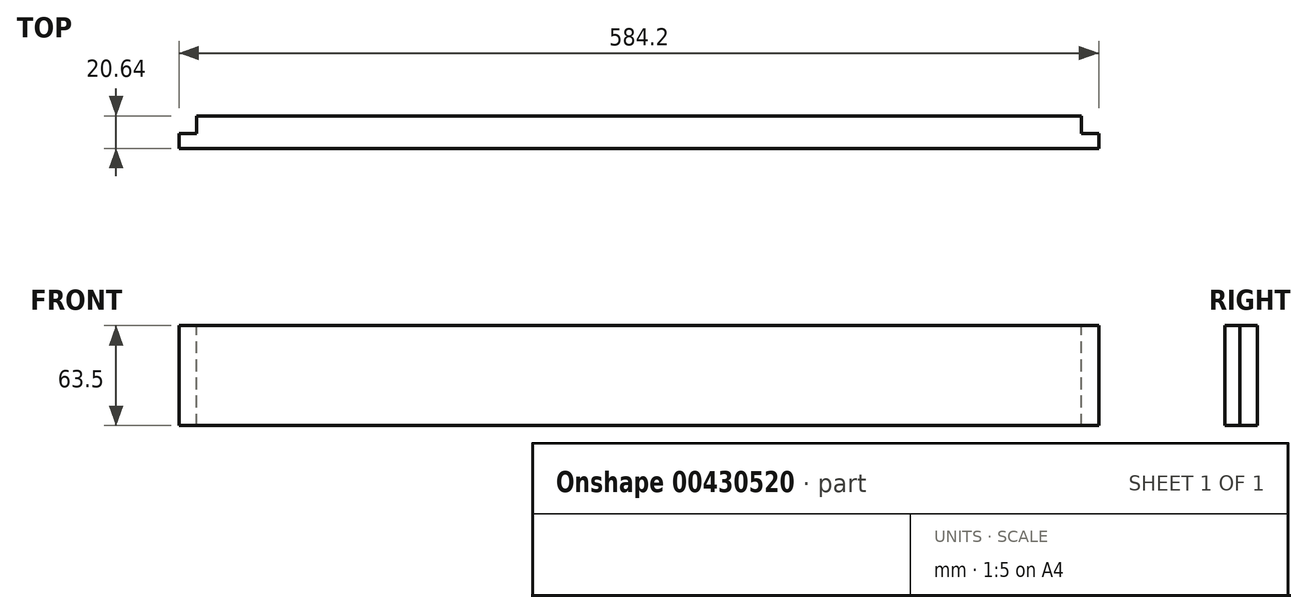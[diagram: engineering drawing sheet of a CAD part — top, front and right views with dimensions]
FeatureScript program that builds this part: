
annotation { "Feature Type Name" : "Feature", "Feature Type Description" : "" }
export const myFeature = defineFeature(function(context is Context, id is Id, definition is map)
    precondition{}
    {
        {
            var Q0;
            Q0=qCreatedBy(makeId("Top.planeOp"),FACE);
            var sketch = newSketch(context, id + "F0", { "sketchPlane" : qUnion([Q0])});
            skLineSegment(sketch, "E0", {"start": v(-292.1, 0) * mm, "end": v(292.1, 0) * mm});
            skLineSegment(sketch, "E1", {"start": v(292.1, 0) * mm, "end": v(292.1, 20.64) * mm});
            skLineSegment(sketch, "E2", {"start": v(292.1, 20.64) * mm, "end": v(-292.1, 20.64) * mm});
            skLineSegment(sketch, "E3", {"start": v(-292.1, 20.64) * mm, "end": v(-292.1, 0) * mm});
            skSolve(sketch);
        }
        {
            var Q0;
            Q0=makeQuery(id+"F0.imprint","IMPRINT",FACE,{"disambiguationData":[TD([[makeQuery(id+"F0.imprint","IMPRINT",EDGE,{"derivedFrom":sQuery(id+"F0.wireOp",EDGE,"E0")}),1.0]])]});
            extrude(context, id + "F1", {"entities" : qUnion([Q0]), "oppositeDirection" : true, "depth" : 63.5 * mm});
        }
        {
            var Q0;
            Q0=makeQuery(id+"F1.opExtrude","CAP_FACE",FACE,{"disambiguationData":[OSD([sQuery(id+"F0.wireOp",EDGE,"E0"),sQuery(id+"F0.wireOp",EDGE,"E1"),sQuery(id+"F0.wireOp",EDGE,"E2"),sQuery(id+"F0.wireOp",EDGE,"E3")])],"isStart":true});
            var sketch = newSketch(context, id + "F2", { "sketchPlane" : qUnion([Q0])});
            skLineSegment(sketch, "E4.bottom", {"start": v(-292.1, 20.64) * mm, "end": v(-280.99, 20.64) * mm});
            skLineSegment(sketch, "E4.top", {"start": v(-292.1, 9.52) * mm, "end": v(-280.99, 9.52) * mm});
            skLineSegment(sketch, "E4.left", {"start": v(-292.1, 20.64) * mm, "end": v(-292.1, 9.52) * mm});
            skLineSegment(sketch, "E4.right", {"start": v(-280.99, 20.64) * mm, "end": v(-280.99, 9.52) * mm});
            skLineSegment(sketch, "E5.bottom", {"start": v(292.1, 20.64) * mm, "end": v(280.99, 20.64) * mm});
            skLineSegment(sketch, "E5.top", {"start": v(292.1, 9.52) * mm, "end": v(280.99, 9.52) * mm});
            skLineSegment(sketch, "E5.left", {"start": v(292.1, 20.64) * mm, "end": v(292.1, 9.52) * mm});
            skLineSegment(sketch, "E5.right", {"start": v(280.99, 20.64) * mm, "end": v(280.99, 9.52) * mm});
            skSolve(sketch);
        }
        {
            var Q0;
            Q0=makeQuery(id+"F2.imprint","IMPRINT",FACE,{"disambiguationData":[TD([[makeQuery(id+"F2.imprint","IMPRINT",EDGE,{"derivedFrom":sQuery(id+"F2.wireOp",EDGE,"E5.bottom")}),1.0]])]});
            var Q1;
            Q1=makeQuery(id+"F2.imprint","IMPRINT",FACE,{"disambiguationData":[TD([[makeQuery(id+"F2.imprint","IMPRINT",EDGE,{"derivedFrom":sQuery(id+"F2.wireOp",EDGE,"E4.bottom")}),1.0]])]});
            extrude(context, id + "F3", {"entities" : qUnion([Q0, Q1]), "operationType" : NewBodyOperationType.REMOVE, "endBound" : BoundingType.THROUGH_ALL, "oppositeDirection" : true, "depth" : 25.4 * mm});
        }
    });
